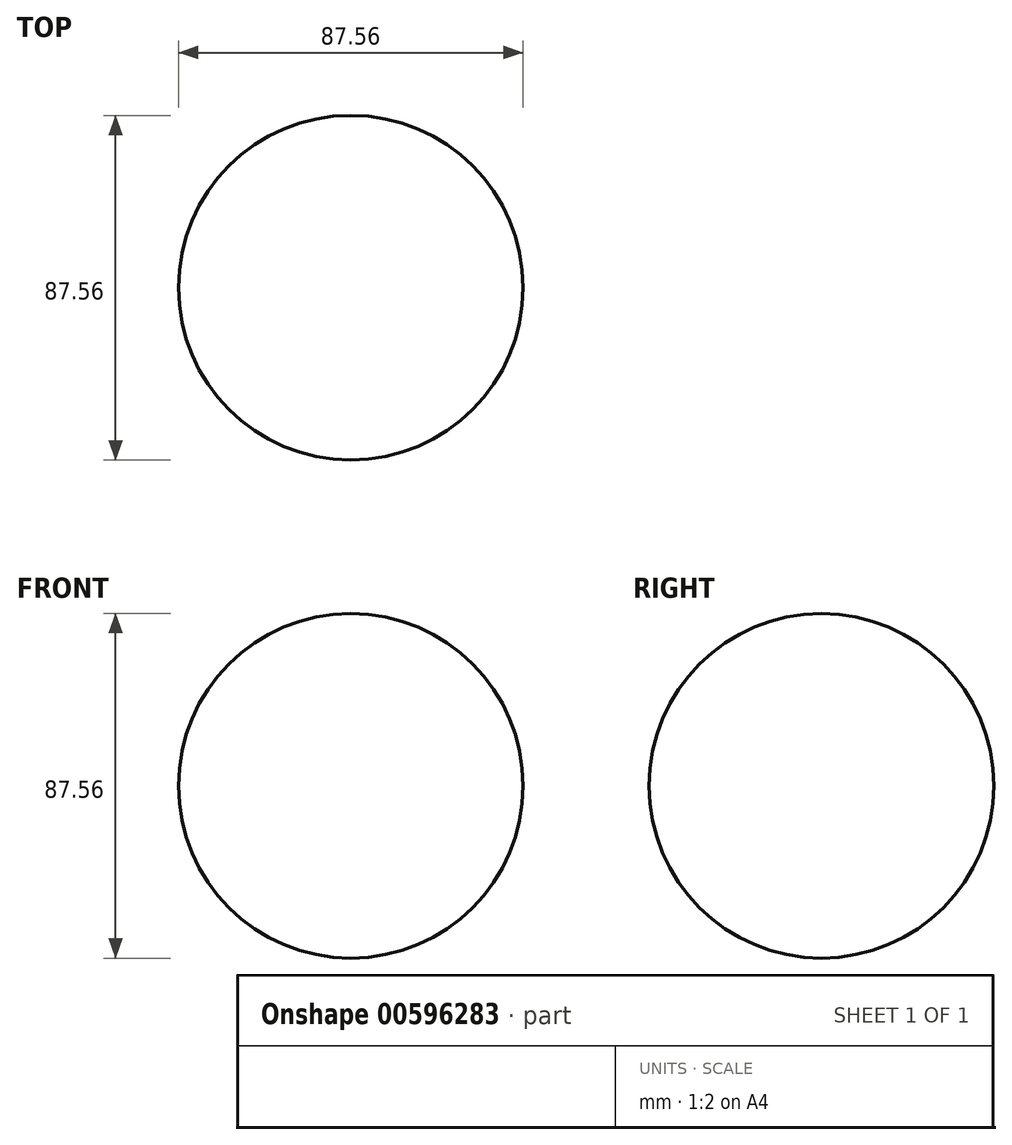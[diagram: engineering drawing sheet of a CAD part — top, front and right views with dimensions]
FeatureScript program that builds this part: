
annotation { "Feature Type Name" : "Feature", "Feature Type Description" : "" }
export const myFeature = defineFeature(function(context is Context, id is Id, definition is map)
    precondition{}
    {
        {
            var Q0;
            Q0=qCreatedBy(makeId("Front.planeOp"),FACE);
            var sketch = newSketch(context, id + "F0", { "sketchPlane" : qUnion([Q0])});
            skArc(sketch, "E0", {"start": v(0, -43.78) * mm, "mid": v(43.78, 0) * mm, "end": v(0, 43.78) * mm});
            skLineSegment(sketch, "E1", {"start": v(0, 48.72) * mm, "end": v(0, -49.3) * mm});
            skSolve(sketch);
        }
        {
            var Q0;
            Q0=qCreatedBy(makeId("Front.planeOp"),FACE);
            var sketch = newSketch(context, id + "F1", { "sketchPlane" : qUnion([Q0])});
            skLineSegment(sketch, "E2", {"start": v(0, 61.07) * mm, "end": v(0, -61.94) * mm});
            skSolve(sketch);
        }
        {
            var Q0;
            Q0 = qSketchRegion(id + "F0", true);
            var Q1;
            Q1=sQuery(id+"F1.wireOp",EDGE,"E2");
            revolve(context, id + "F2", {"entities" : qUnion([Q0]), "axis" : qUnion([Q1]), "revolveType" : RevolveType.FULL});
        }
    });
